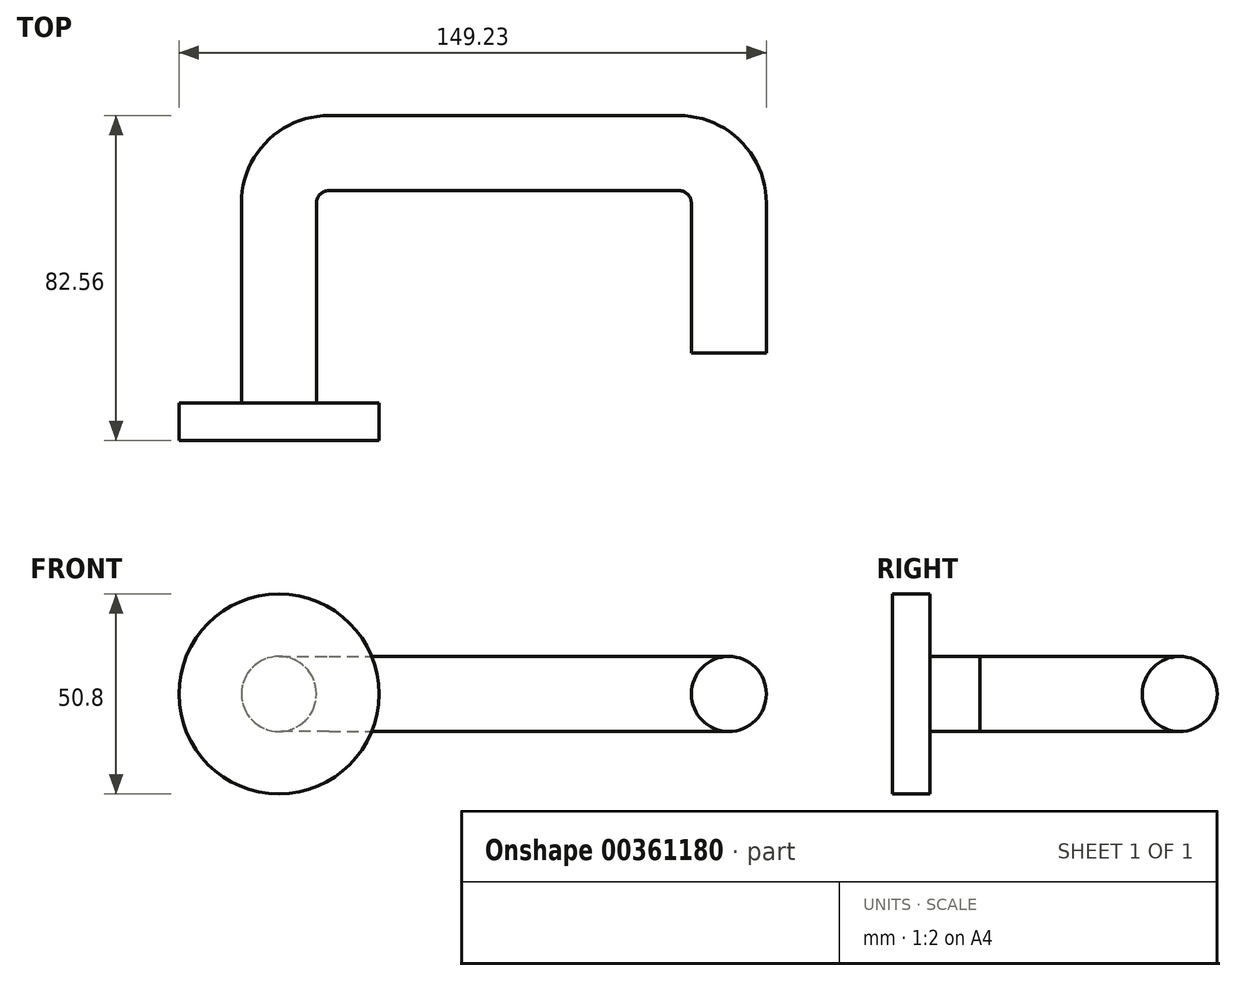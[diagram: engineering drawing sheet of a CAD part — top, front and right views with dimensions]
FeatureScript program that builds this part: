
annotation { "Feature Type Name" : "Feature", "Feature Type Description" : "" }
export const myFeature = defineFeature(function(context is Context, id is Id, definition is map)
    precondition{}
    {
        {
            var Q0;
            Q0=qCreatedBy(makeId("Front.planeOp"),FACE);
            var sketch = newSketch(context, id + "F0", { "sketchPlane" : qUnion([Q0])});
            skCircle(sketch, "E0", {"center": v(0, 0) * mm, "radius": 25.4 * mm});
            skSolve(sketch);
        }
        {
            var Q0;
            Q0=makeQuery(id+"F0.imprint","IMPRINT",FACE,{"disambiguationData":[TD([[makeQuery(id+"F0.imprint","IMPRINT",EDGE,{"derivedFrom":sQuery(id+"F0.wireOp",EDGE,"E0")}),1.0]])]});
            extrude(context, id + "F1", {"entities" : qUnion([Q0]), "depth" : 9.52 * mm});
        }
        {
            var Q0;
            Q0=qCreatedBy(makeId("Top.planeOp"),FACE);
            var sketch = newSketch(context, id + "F2", { "sketchPlane" : qUnion([Q0])});
            skLineSegment(sketch, "E1", {"start": v(0, 0) * mm, "end": v(0, 50.8) * mm});
            skArc(sketch, "E2", {"start": v(12.7, 63.5) * mm, "mid": v(3.72, 59.78) * mm, "end": v(0, 50.8) * mm});
            skLineSegment(sketch, "E3", {"start": v(12.7, 63.5) * mm, "end": v(101.6, 63.5) * mm});
            skArc(sketch, "E4", {"start": v(114.3, 50.8) * mm, "mid": v(110.58, 59.78) * mm, "end": v(101.6, 63.5) * mm});
            skLineSegment(sketch, "E5", {"start": v(114.3, 50.8) * mm, "end": v(114.3, 12.7) * mm});
            skSolve(sketch);
        }
        {
            var Q0;
            Q0=makeQuery(id+"F1.opExtrude","CAP_FACE",FACE,{"disambiguationData":[OSD([sQuery(id+"F0.wireOp",EDGE,"E0")])],"isStart":true});
            var sketch = newSketch(context, id + "F3", { "sketchPlane" : qUnion([Q0])});
            skCircle(sketch, "E6", {"center": v(0, 0) * mm, "radius": 9.53 * mm});
            skSolve(sketch);
        }
        {
            var Q0;
            Q0=makeQuery(id+"F3.imprint","IMPRINT",FACE,{"disambiguationData":[TD([[makeQuery(id+"F3.imprint","IMPRINT",EDGE,{"derivedFrom":sQuery(id+"F3.wireOp",EDGE,"E6")}),1.0]])]});
            var Q1;
            Q1=sQuery(id+"F2.wireOp",EDGE,"E1");
            var Q2;
            Q2=sQuery(id+"F2.wireOp",EDGE,"E2");
            var Q3;
            Q3=sQuery(id+"F2.wireOp",EDGE,"E3");
            var Q4;
            Q4=sQuery(id+"F2.wireOp",EDGE,"E4");
            var Q5;
            Q5=sQuery(id+"F2.wireOp",EDGE,"E5");
            sweep(context, id + "F4", {"operationType" : NewBodyOperationType.ADD, "profiles" : qUnion([Q0]), "path" : qUnion([Q1, Q2, Q3, Q4, Q5])});
        }
    });
